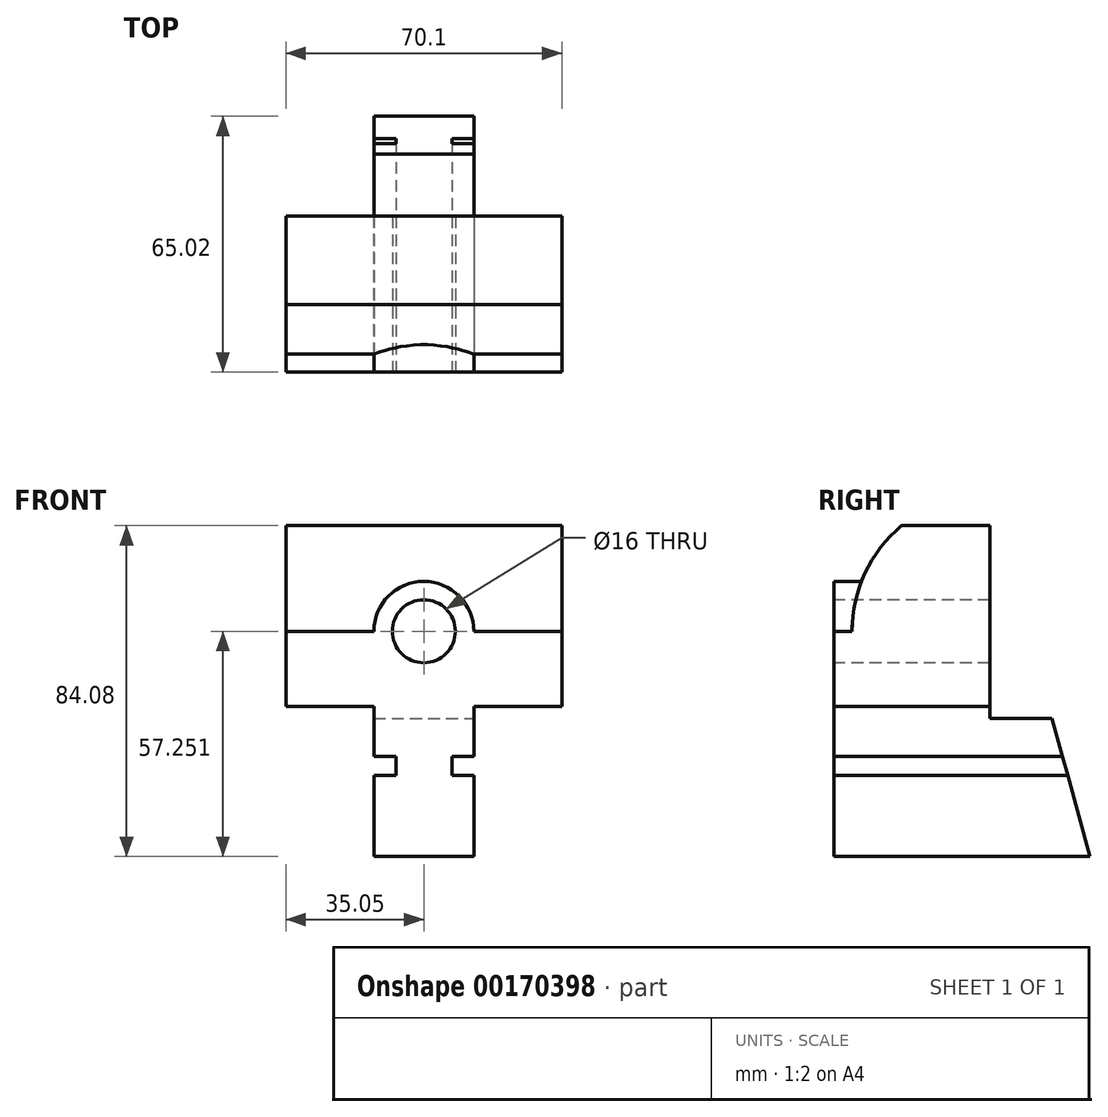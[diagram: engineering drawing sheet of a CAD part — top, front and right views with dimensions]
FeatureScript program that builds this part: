
annotation { "Feature Type Name" : "Feature", "Feature Type Description" : "" }
export const myFeature = defineFeature(function(context is Context, id is Id, definition is map)
    precondition{}
    {
        {
            var Q0;
            Q0=qCreatedBy(makeId("Right.planeOp"),FACE);
            var sketch = newSketch(context, id + "F0", { "sketchPlane" : qUnion([Q0])});
            skLineSegment(sketch, "E0.bottom", {"start": v(-32.51, 42.04) * mm, "end": v(32.51, 42.04) * mm});
            skLineSegment(sketch, "E0.top", {"start": v(-32.51, -42.04) * mm, "end": v(32.51, -42.04) * mm});
            skLineSegment(sketch, "E0.left", {"start": v(-32.51, 42.04) * mm, "end": v(-32.51, -42.04) * mm});
            skLineSegment(sketch, "E0.right", {"start": v(32.51, 42.04) * mm, "end": v(32.51, -42.04) * mm});
            skPoint(sketch, "E0.middle", {"position": v(0, 0) * mm});
            skSolve(sketch);
        }
        {
            var Q0;
            Q0=makeQuery(id+"F0.imprint","IMPRINT",FACE,{"disambiguationData":[TD([[makeQuery(id+"F0.imprint","IMPRINT",EDGE,{"derivedFrom":sQuery(id+"F0.wireOp",EDGE,"E0.bottom")}),-1.0]])]});
            extrude(context, id + "F1", {"entities" : qUnion([Q0]), "endBound" : BoundingType.SYMMETRIC, "depth" : 70.1 * mm});
        }
        {
            var Q0;
            Q0=qCreatedBy(makeId("Front.planeOp"),FACE);
            var sketch = newSketch(context, id + "F2", { "sketchPlane" : qUnion([Q0])});
            skLineSegment(sketch, "E1.bottom", {"start": v(-44.45, -71.3) * mm, "end": v(-12.7, -71.3) * mm});
            skLineSegment(sketch, "E1.top", {"start": v(-44.45, -3.94) * mm, "end": v(-12.7, -3.94) * mm});
            skLineSegment(sketch, "E1.left", {"start": v(-44.45, -71.3) * mm, "end": v(-44.45, -3.94) * mm});
            skLineSegment(sketch, "E1.right", {"start": v(-12.7, -71.3) * mm, "end": v(-12.7, -3.94) * mm});
            skLineSegment(sketch, "E2", {"start": v(-12.7, -3.94) * mm, "end": v(12.7, -3.94) * mm, "construction": true});
            skLineSegment(sketch, "E3.bottom", {"start": v(12.7, -3.94) * mm, "end": v(44.45, -3.94) * mm});
            skLineSegment(sketch, "E3.top", {"start": v(12.7, -71.19) * mm, "end": v(44.45, -71.19) * mm});
            skLineSegment(sketch, "E3.left", {"start": v(12.7, -3.94) * mm, "end": v(12.7, -71.19) * mm});
            skLineSegment(sketch, "E3.right", {"start": v(44.45, -3.94) * mm, "end": v(44.45, -71.19) * mm});
            skLineSegment(sketch, "E4", {"start": v(-12.7, -16.64) * mm, "end": v(-7.11, -16.64) * mm});
            skLineSegment(sketch, "E5", {"start": v(-7.11, -16.64) * mm, "end": v(-7.11, -21.46) * mm});
            skLineSegment(sketch, "E6", {"start": v(-7.11, -21.46) * mm, "end": v(-12.7, -21.46) * mm});
            skLineSegment(sketch, "E7", {"start": v(12.7, -16.64) * mm, "end": v(7.11, -16.64) * mm});
            skLineSegment(sketch, "E8", {"start": v(7.11, -16.64) * mm, "end": v(7.11, -21.46) * mm});
            skLineSegment(sketch, "E9", {"start": v(7.11, -21.46) * mm, "end": v(12.7, -21.46) * mm});
            skSolve(sketch);
        }
        {
            var Q0;
            Q0 = qSketchRegion(id + "F2", true);
            extrude(context, id + "F3", {"entities" : qUnion([Q0]), "operationType" : NewBodyOperationType.REMOVE, "endBound" : BoundingType.SYMMETRIC, "oppositeDirection" : true, "depth" : 254 * mm});
        }
        {
            var Q0;
            Q0=qCreatedBy(makeId("Right.planeOp"),FACE);
            var sketch = newSketch(context, id + "F4", { "sketchPlane" : qUnion([Q0])});
            skLineSegment(sketch, "E10.bottom", {"start": v(7.11, 62.33) * mm, "end": v(69.79, 62.33) * mm});
            skLineSegment(sketch, "E10.top", {"start": v(7.11, -6.99) * mm, "end": v(69.79, -6.99) * mm});
            skLineSegment(sketch, "E10.left", {"start": v(7.11, 62.33) * mm, "end": v(7.11, -6.99) * mm});
            skLineSegment(sketch, "E10.right", {"start": v(69.79, 62.33) * mm, "end": v(69.79, -6.99) * mm});
            skSolve(sketch);
        }
        {
            var Q0;
            Q0 = qSketchRegion(id + "F4", true);
            extrude(context, id + "F5", {"entities" : qUnion([Q0]), "operationType" : NewBodyOperationType.REMOVE, "endBound" : BoundingType.SYMMETRIC, "oppositeDirection" : true, "depth" : 254 * mm});
        }
        {
            var Q0;
            {var subQ0=sQuery(id+"F2.wireOp",EDGE,"E3.left");Q0=makeQuery(id+"F3.boolean.opBoolean","COPY",FACE,{"derivedFrom":makeQuery(id+"F3.opExtrude","SWEPT_FACE",FACE,{"disambiguationData":[OSD([subQ0]),TDD([makeQuery(id+"F2.imprint","IMPRINT",EDGE,{"disambiguationData":[TD([[makeQuery(id+"F2.imprint","INTERSECT",VERTEX,{"derivedFrom":[sQuery(id+"F2.wireOp",EDGE,"E3.top"),subQ0]}),1.0]])],"derivedFrom":subQ0})])]})});}
            var sketch = newSketch(context, id + "F6", { "sketchPlane" : qUnion([Q0])});
            skLineSegment(sketch, "E11", {"start": v(32.51, -42.04) * mm, "end": v(22.86, -6.99) * mm});
            skLineSegment(sketch, "E12", {"start": v(22.86, -6.99) * mm, "end": v(47.05, -1.72) * mm});
            skLineSegment(sketch, "E13", {"start": v(47.05, -1.72) * mm, "end": v(51.48, -29.32) * mm});
            skLineSegment(sketch, "E14", {"start": v(51.48, -29.32) * mm, "end": v(32.51, -42.04) * mm});
            skSolve(sketch);
        }
        {
            var Q0;
            Q0 = qSketchRegion(id + "F6", true);
            extrude(context, id + "F7", {"entities" : qUnion([Q0]), "operationType" : NewBodyOperationType.REMOVE, "endBound" : BoundingType.SYMMETRIC, "oppositeDirection" : true, "depth" : 254 * mm});
        }
        {
            var Q0;
            Q0=qCreatedBy(makeId("Right.planeOp"),FACE);
            var sketch = newSketch(context, id + "F8", { "sketchPlane" : qUnion([Q0])});
            skCircle(sketch, "E15", {"center": v(7.11, 15.11) * mm, "radius": 35.05 * mm});
            skLineSegment(sketch, "E16", {"start": v(-27.94, 15.21) * mm, "end": v(-50.78, 15.21) * mm});
            skLineSegment(sketch, "E17", {"start": v(-50.78, 15.21) * mm, "end": v(-42.65, 55.48) * mm});
            skLineSegment(sketch, "E18", {"start": v(-42.65, 55.48) * mm, "end": v(6.9, 50.16) * mm});
            skSolve(sketch);
        }
        {
            var Q0;
            {var subQ0=sQuery(id+"F8.wireOp",EDGE,"E16");Q0=makeQuery(id+"F8.imprint","IMPRINT",FACE,{"disambiguationData":[TD([[makeQuery(id+"F8.imprint","IMPRINT",EDGE,{"derivedFrom":subQ0}),-1.0]])]});}
            extrude(context, id + "F9", {"entities" : qUnion([Q0]), "operationType" : NewBodyOperationType.REMOVE, "endBound" : BoundingType.SYMMETRIC, "oppositeDirection" : true, "depth" : 254 * mm});
        }
        {
            var Q0;
            Q0=makeQuery(id+"F1.opExtrude","SWEPT_FACE",FACE,{"disambiguationData":[OSD([sQuery(id+"F0.wireOp",EDGE,"E0.left")])]});
            var sketch = newSketch(context, id + "F10", { "sketchPlane" : qUnion([Q0])});
            skCircle(sketch, "E19", {"center": v(0, 15.21) * mm, "radius": 12.7 * mm});
            skSolve(sketch);
        }
        {
            var Q0;
            {var subQ0=sQuery(id+"F10.wireOp",EDGE,"E19");var subQ1=makeQuery(id+"F9.boolean.opBoolean","INTERSECT",EDGE,{"derivedFrom":[makeQuery(id+"F1.opExtrude","SWEPT_FACE",FACE,{"disambiguationData":[OSD([sQuery(id+"F0.wireOp",EDGE,"E0.left")])]}),makeQuery(id+"F9.opExtrude","SWEPT_FACE",FACE,{"disambiguationData":[OSD([sQuery(id+"F8.wireOp",EDGE,"E16")])]})]});var subQ2=makeQuery(id+"F10.imprint","INTERSECT",VERTEX,{"disambiguationData":[OD(0.0)],"derivedFrom":[subQ1,subQ0]});Q0=makeQuery(id+"F10.imprint","IMPRINT",FACE,{"disambiguationData":[TD([[makeQuery(id+"F10.imprint","IMPRINT",EDGE,{"disambiguationData":[TD([[subQ2,1.0]])],"derivedFrom":subQ0}),1.0]])]});}
            var Q1;
            {var subQ0=sQuery(id+"F10.wireOp",EDGE,"E19");var subQ1=makeQuery(id+"F9.boolean.opBoolean","INTERSECT",EDGE,{"derivedFrom":[makeQuery(id+"F1.opExtrude","SWEPT_FACE",FACE,{"disambiguationData":[OSD([sQuery(id+"F0.wireOp",EDGE,"E0.left")])]}),makeQuery(id+"F9.opExtrude","SWEPT_FACE",FACE,{"disambiguationData":[OSD([sQuery(id+"F8.wireOp",EDGE,"E16")])]})]});var subQ2=makeQuery(id+"F10.imprint","INTERSECT",VERTEX,{"disambiguationData":[OD(0.0)],"derivedFrom":[subQ1,subQ0]});Q1=makeQuery(id+"F10.imprint","IMPRINT",FACE,{"disambiguationData":[TD([[makeQuery(id+"F10.imprint","IMPRINT",EDGE,{"disambiguationData":[TD([[subQ2,-1.0]])],"derivedFrom":subQ0}),1.0]])]});}
            extrude(context, id + "F11", {"entities" : qUnion([Q0, Q1]), "operationType" : NewBodyOperationType.ADD, "oppositeDirection" : true, "depth" : 25.4 * mm});
        }
        {
            var Q0;
            Q0=makeQuery(id+"F11.boolean.opBoolean","MERGE",FACE,{"derivedFrom":[makeQuery(id+"F1.opExtrude","SWEPT_FACE",FACE,{"disambiguationData":[OSD([sQuery(id+"F0.wireOp",EDGE,"E0.left")])]}),makeQuery(id+"F11.opExtrude","CAP_FACE",FACE,{"disambiguationData":[OSD([sQuery(id+"F10.wireOp",EDGE,"E19")])],"isStart":true})]});
            var sketch = newSketch(context, id + "F12", { "sketchPlane" : qUnion([Q0])});
            skCircle(sketch, "E20", {"center": v(0, 15.21) * mm, "radius": 8 * mm});
            skSolve(sketch);
        }
        {
            var Q0;
            Q0=makeQuery(id+"F12.imprint","IMPRINT",FACE,{"disambiguationData":[TD([[makeQuery(id+"F12.imprint","IMPRINT",EDGE,{"derivedFrom":sQuery(id+"F12.wireOp",EDGE,"E20")}),1.0]])]});
            extrude(context, id + "F13", {"entities" : qUnion([Q0]), "operationType" : NewBodyOperationType.REMOVE, "endBound" : BoundingType.THROUGH_ALL, "oppositeDirection" : true, "depth" : 25.4 * mm});
        }
    });
